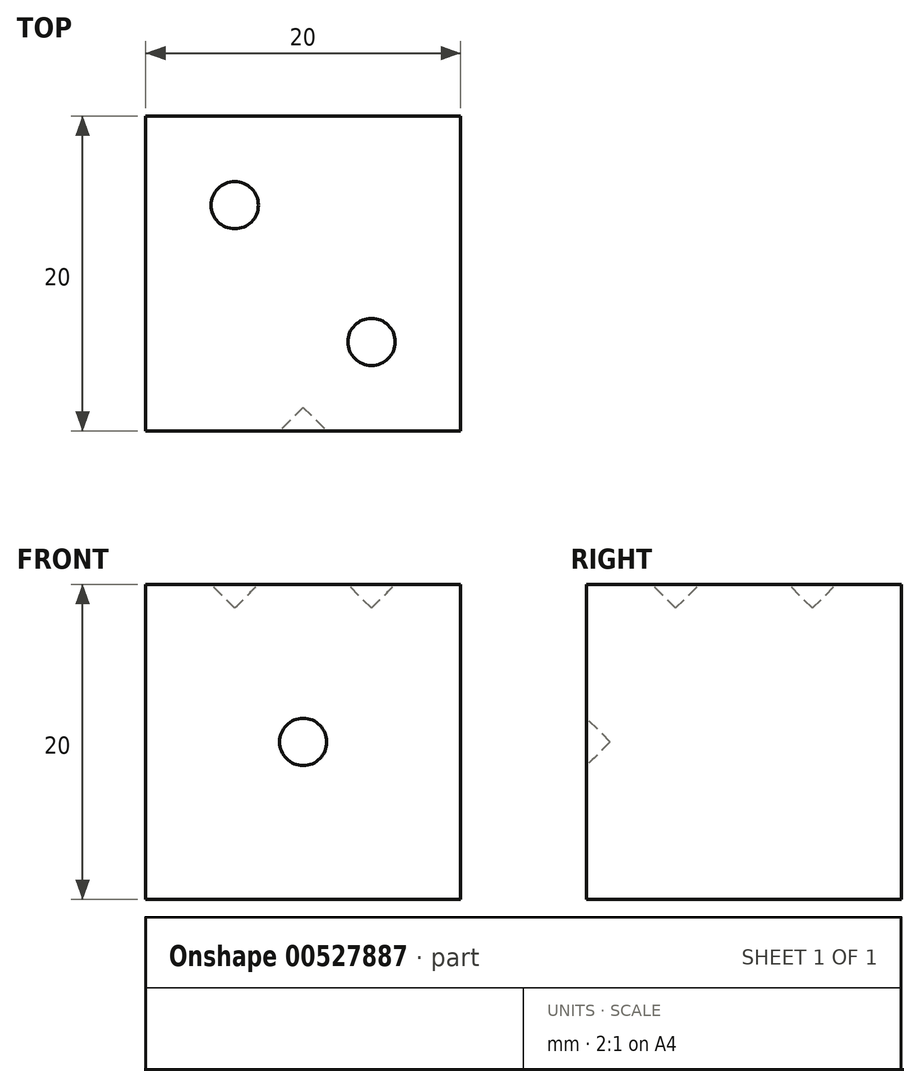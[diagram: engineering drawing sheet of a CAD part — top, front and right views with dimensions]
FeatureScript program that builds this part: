
annotation { "Feature Type Name" : "Feature", "Feature Type Description" : "" }
export const myFeature = defineFeature(function(context is Context, id is Id, definition is map)
    precondition{}
    {
        {
            var Q0;
            Q0=qCreatedBy(makeId("Top.planeOp"),FACE);
            var sketch = newSketch(context, id + "F0", { "sketchPlane" : qUnion([Q0])});
            skLineSegment(sketch, "E0.bottom", {"start": v(0, 0) * mm, "end": v(20, 0) * mm});
            skLineSegment(sketch, "E0.top", {"start": v(0, 20) * mm, "end": v(20, 20) * mm});
            skLineSegment(sketch, "E0.left", {"start": v(0, 0) * mm, "end": v(0, 20) * mm});
            skLineSegment(sketch, "E0.right", {"start": v(20, 0) * mm, "end": v(20, 20) * mm});
            skSolve(sketch);
        }
        {
            var Q0;
            Q0=qSketchRegion(id+"F0",true);
            extrude(context, id + "F1", {"entities" : qUnion([Q0]), "depth" : 20 * mm});
        }
        {
            var Q0;
            Q0=makeQuery(id+"F1.opExtrude","SWEPT_FACE",FACE,{"disambiguationData":[OSD([sQuery(id+"F0.wireOp",EDGE,"E0.bottom")])]});
            var sketch = newSketch(context, id + "F2", { "sketchPlane" : qUnion([Q0])});
            skLineSegment(sketch, "E1", {"start": v(10, 20) * mm, "end": v(10, 0) * mm, "construction": true});
            skCircle(sketch, "E2", {"center": v(10, 10) * mm, "radius": 1.5 * mm});
            skSolve(sketch);
        }
        {
            var Q0;
            Q0=qSketchRegion(id+"F2",true);
            extrude(context, id + "F3", {"entities" : qUnion([Q0]), "operationType" : NewBodyOperationType.REMOVE, "oppositeDirection" : true, "depth" : 1.5 * mm});
        }
        {
            var Q0;
            Q0=makeQuery(id+"F1.opExtrude","CAP_FACE",FACE,{"disambiguationData":[OSD([sQuery(id+"F0.wireOp",EDGE,"E0.bottom"),sQuery(id+"F0.wireOp",EDGE,"E0.top"),sQuery(id+"F0.wireOp",EDGE,"E0.left"),sQuery(id+"F0.wireOp",EDGE,"E0.right")])],"isStart":false});
            var sketch = newSketch(context, id + "F4", { "sketchPlane" : qUnion([Q0])});
            skLineSegment(sketch, "E3", {"start": v(0, 20) * mm, "end": v(5.66, 14.34) * mm, "construction": true});
            skLineSegment(sketch, "E4", {"start": v(20, 0) * mm, "end": v(14.34, 5.66) * mm, "construction": true});
            skCircle(sketch, "E5", {"center": v(5.66, 14.34) * mm, "radius": 1.5 * mm});
            skCircle(sketch, "E6", {"center": v(14.34, 5.66) * mm, "radius": 1.5 * mm});
            skSolve(sketch);
        }
        {
            var Q0;
            Q0=qSketchRegion(id+"F4",true);
            extrude(context, id + "F5", {"entities" : qUnion([Q0]), "operationType" : NewBodyOperationType.REMOVE, "oppositeDirection" : true, "depth" : 1.5 * mm});
        }
        {
            var Q0;
            Q0=makeQuery(id+"F3.boolean.opBoolean","COPY",EDGE,{"derivedFrom":makeQuery(id+"F3.opExtrude","CAP_EDGE",EDGE,{"disambiguationData":[OSD([sQuery(id+"F2.wireOp",EDGE,"E2")])],"isStart":false})});
            var Q1;
            Q1=makeQuery(id+"F5.boolean.opBoolean","COPY",EDGE,{"derivedFrom":makeQuery(id+"F5.opExtrude","CAP_EDGE",EDGE,{"disambiguationData":[OSD([sQuery(id+"F4.wireOp",EDGE,"E5")])],"isStart":false})});
            var Q2;
            Q2=makeQuery(id+"F5.boolean.opBoolean","COPY",EDGE,{"derivedFrom":makeQuery(id+"F5.opExtrude","CAP_EDGE",EDGE,{"disambiguationData":[OSD([sQuery(id+"F4.wireOp",EDGE,"E6")])],"isStart":false})});
            chamfer(context, id + "F6", {"entities" : qUnion([Q0, Q1, Q2]), "width" : 1.5 * mm, "tangentPropagation" : true});
        }
    });
